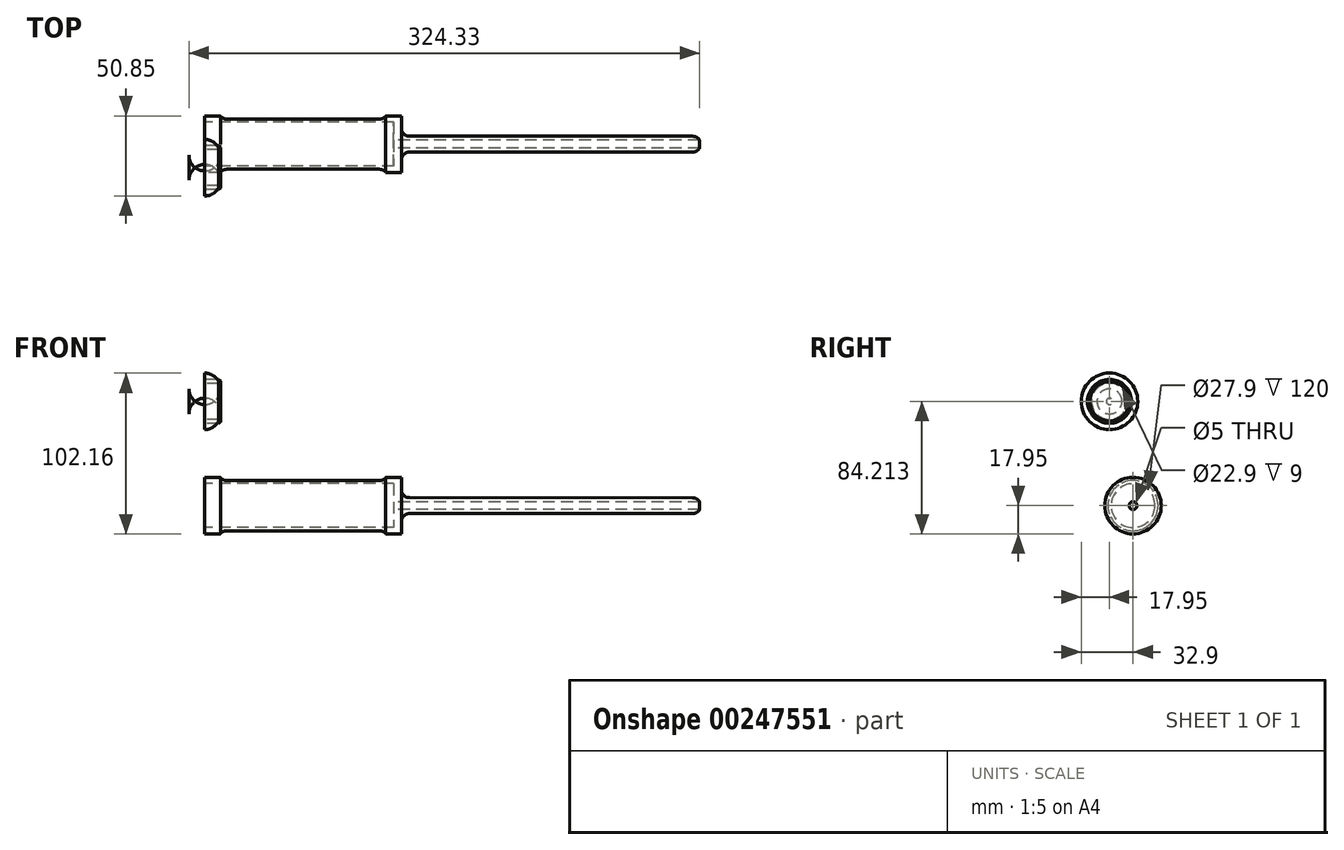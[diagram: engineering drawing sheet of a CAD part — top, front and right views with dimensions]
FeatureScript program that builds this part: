
annotation { "Feature Type Name" : "Feature", "Feature Type Description" : "" }
export const myFeature = defineFeature(function(context is Context, id is Id, definition is map)
    precondition{}
    {
        {
            var Q0;
            Q0=qCreatedBy(makeId("Top.planeOp"),FACE);
            var sketch = newSketch(context, id + "F0", { "sketchPlane" : qUnion([Q0])});
            skLineSegment(sketch, "E0", {"start": v(0, 32.9) * mm, "end": v(10, 32.9) * mm});
            skLineSegment(sketch, "E1", {"start": v(10, 32.9) * mm, "end": v(10, 30.9) * mm});
            skLineSegment(sketch, "E2", {"start": v(10, 30.9) * mm, "end": v(115, 30.9) * mm});
            skLineSegment(sketch, "E3", {"start": v(115, 30.9) * mm, "end": v(115, 32.9) * mm});
            skLineSegment(sketch, "E4", {"start": v(115, 32.9) * mm, "end": v(125, 32.9) * mm});
            skLineSegment(sketch, "E5", {"start": v(125, 14.95) * mm, "end": v(315, 14.95) * mm});
            skLineSegment(sketch, "E6", {"start": v(315, 14.95) * mm, "end": v(315, 19.95) * mm});
            skLineSegment(sketch, "E7", {"start": v(315, 19.95) * mm, "end": v(125, 20) * mm});
            skLineSegment(sketch, "E8", {"start": v(0, 32.9) * mm, "end": v(0, 14.95) * mm});
            skLineSegment(sketch, "E9", {"start": v(0, 14.95) * mm, "end": v(125, 14.95) * mm});
            skLineSegment(sketch, "E10", {"start": v(125, 32.9) * mm, "end": v(125, 20) * mm});
            skSolve(sketch);
        }
        {
            var Q0;
            Q0 = qSketchRegion(id + "F0", true);
            var Q1;
            Q1=sQuery(id+"F0.wireOp",EDGE,"E9");
            revolve(context, id + "F1", {"entities" : qUnion([Q0]), "axis" : qUnion([Q1]), "revolveType" : RevolveType.FULL});
        }
        {
            var Q0;
            Q0=makeQuery(id+"F1.opRevolve","SWEPT_FACE",FACE,{"disambiguationData":[OSD([sQuery(id+"F0.wireOp",EDGE,"E2")])]});
            var Q1;
            Q1=makeQuery(id+"F1.opRevolve","SWEPT_FACE",FACE,{"disambiguationData":[OSD([sQuery(id+"F0.wireOp",EDGE,"E7")])]});
            fillet(context, id + "F2", {"entities" : qUnion([Q0, Q1]), "radius" : 5 * mm, "tangentPropagation" : true, "allowEdgeOverflow" : false});
        }
        {
            var Q0;
            Q0=makeQuery(id+"F1.opRevolve","SWEPT_FACE",FACE,{"disambiguationData":[OSD([sQuery(id+"F0.wireOp",EDGE,"E8")])]});
            var sketch = newSketch(context, id + "F3", { "sketchPlane" : qUnion([Q0])});
            skCircle(sketch, "E11", {"center": v(-14.95, 0) * mm, "radius": 13.95 * mm});
            skSolve(sketch);
        }
        {
            var Q0;
            Q0 = qSketchRegion(id + "F3", true);
            extrude(context, id + "F4", {"entities" : qUnion([Q0]), "operationType" : NewBodyOperationType.REMOVE, "oppositeDirection" : true, "depth" : 120 * mm});
        }
        {
            var Q0;
            Q0=qCreatedBy(makeId("Right.planeOp"),FACE);
            var sketch = newSketch(context, id + "F5", { "sketchPlane" : qUnion([Q0])});
            skCircle(sketch, "E12", {"center": v(0, 66.26) * mm, "radius": 17.95 * mm});
            skSolve(sketch);
        }
        {
            var Q0;
            Q0 = qSketchRegion(id + "F5", true);
            extrude(context, id + "F6", {"entities" : qUnion([Q0]), "oppositeDirection" : true, "depth" : 10 * mm});
        }
        {
            var Q0;
            Q0=makeQuery(id+"F6.opExtrude","CAP_FACE",FACE,{"disambiguationData":[OSD([sQuery(id+"F5.wireOp",EDGE,"E12")])],"isStart":true});
            var sketch = newSketch(context, id + "F7", { "sketchPlane" : qUnion([Q0])});
            skCircle(sketch, "E13", {"center": v(0, 66.26) * mm, "radius": 13.95 * mm});
            skCircle(sketch, "E14", {"center": v(0, 66.26) * mm, "radius": 11.45 * mm});
            skSolve(sketch);
        }
        {
            var Q0;
            Q0=makeQuery(id+"F7.imprint","IMPRINT",FACE,{"disambiguationData":[TD([[makeQuery(id+"F7.imprint","IMPRINT",EDGE,{"derivedFrom":sQuery(id+"F7.wireOp",EDGE,"E13")}),1.0]])]});
            var Q1;
            Q1=sQuery(id+"F7.wireOp",EDGE,"E14");
            var Q2;
            Q2=sQuery(id+"F7.wireOp",EDGE,"E13");
            extrude(context, id + "F8", {"entities" : qUnion([Q0]), "operationType" : NewBodyOperationType.ADD, "surfaceEntities" : qUnion([Q1, Q2]), "depth" : 10 * mm});
        }
        {
            var Q0;
            Q0=makeQuery(id+"F8.opExtrude","CAP_FACE",FACE,{"disambiguationData":[OSD([sQuery(id+"F7.wireOp",EDGE,"E13"),sQuery(id+"F7.wireOp",EDGE,"E14")])],"isStart":false});
            chamfer(context, id + "F9", {"entities" : qUnion([Q0]), "width" : 1 * mm, "tangentPropagation" : true});
        }
        {
            var Q0;
            Q0=makeQuery(id+"F6.opExtrude","CAP_EDGE",EDGE,{"disambiguationData":[OSD([sQuery(id+"F5.wireOp",EDGE,"E12")])],"isStart":false});
            fillet(context, id + "F10", {"entities" : qUnion([Q0]), "radius" : 10 * mm, "tangentPropagation" : true, "allowEdgeOverflow" : false});
        }
        {
            var Q0;
            Q0=makeQuery(id+"F4.boolean.opBoolean","COPY",FACE,{"derivedFrom":makeQuery(id+"F4.opExtrude","CAP_FACE",FACE,{"disambiguationData":[OSD([sQuery(id+"F3.wireOp",EDGE,"E11")])],"isStart":false})});
            var sketch = newSketch(context, id + "F11", { "sketchPlane" : qUnion([Q0])});
            skCircle(sketch, "E15", {"center": v(-14.95, 0) * mm, "radius": 2.5 * mm});
            skSolve(sketch);
        }
        {
            var Q0;
            Q0=makeQuery(id+"F11.imprint","IMPRINT",FACE,{"disambiguationData":[TD([[makeQuery(id+"F11.imprint","IMPRINT",EDGE,{"derivedFrom":sQuery(id+"F11.wireOp",EDGE,"E15")}),1.0]])]});
            var Q1;
            Q1=sQuery(id+"F11.wireOp",EDGE,"E15");
            extrude(context, id + "F12", {"entities" : qUnion([Q0]), "operationType" : NewBodyOperationType.REMOVE, "surfaceEntities" : qUnion([Q1]), "endBound" : BoundingType.THROUGH_ALL, "oppositeDirection" : true, "depth" : 25 * mm});
        }
    });
